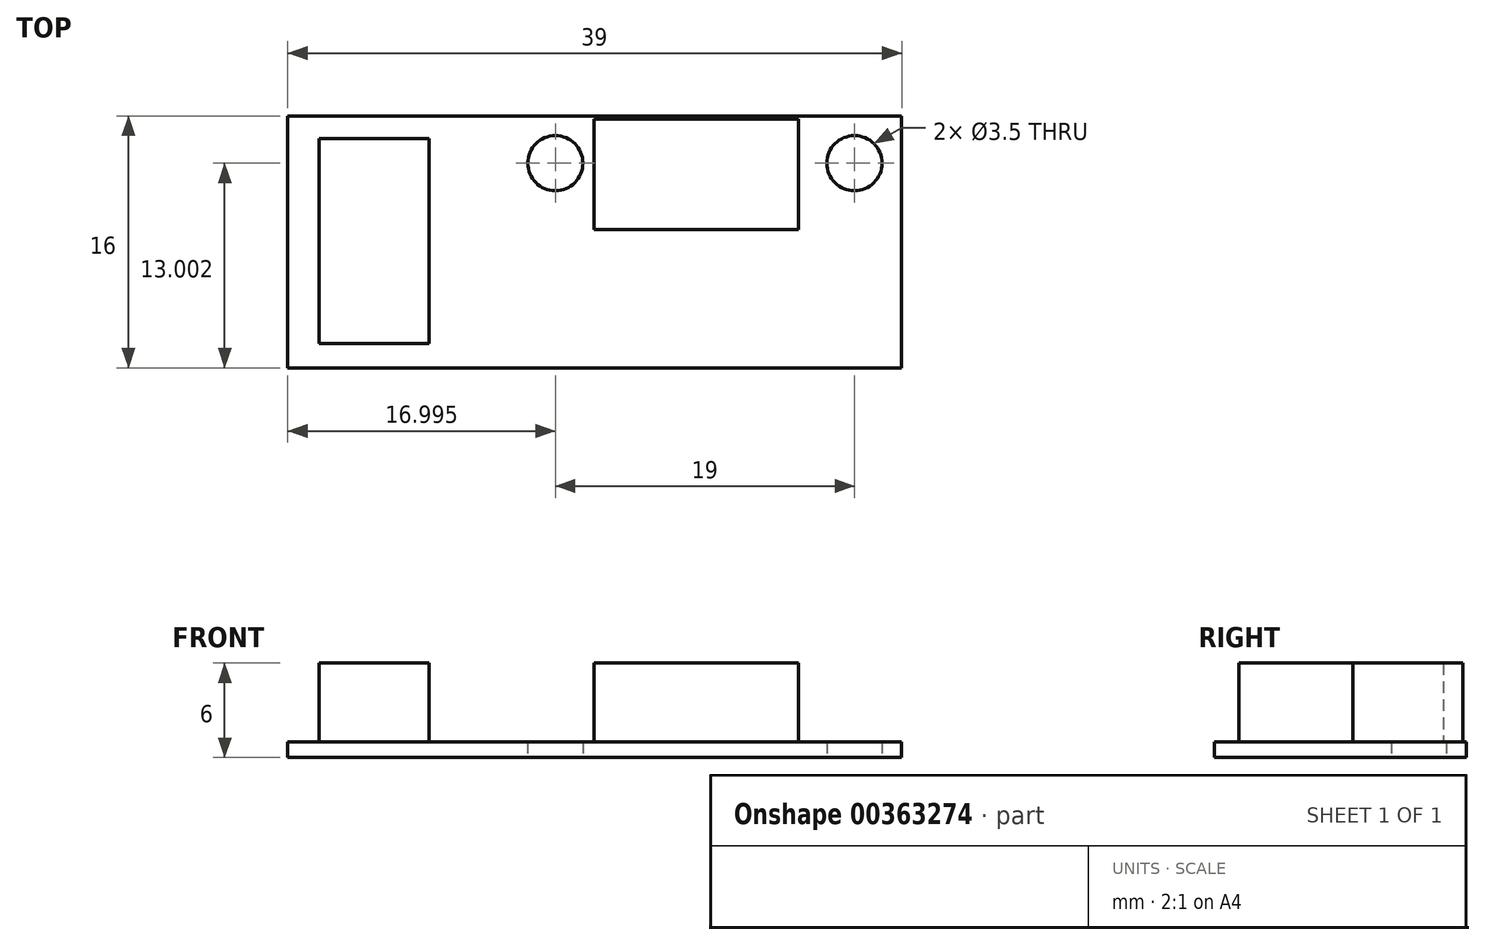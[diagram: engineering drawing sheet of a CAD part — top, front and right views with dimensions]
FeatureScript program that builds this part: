
annotation { "Feature Type Name" : "Feature", "Feature Type Description" : "" }
export const myFeature = defineFeature(function(context is Context, id is Id, definition is map)
    precondition{}
    {
        {
            var Q0;
            Q0=qCreatedBy(makeId("Top.planeOp"),FACE);
            var sketch = newSketch(context, id + "F0", { "sketchPlane" : qUnion([Q0])});
            skLineSegment(sketch, "E0.bottom", {"start": v(-16.63, 6.28) * mm, "end": v(22.37, 6.28) * mm});
            skLineSegment(sketch, "E0.top", {"start": v(-16.63, -9.72) * mm, "end": v(22.37, -9.72) * mm});
            skLineSegment(sketch, "E0.left", {"start": v(-16.63, 6.28) * mm, "end": v(-16.63, -9.72) * mm});
            skLineSegment(sketch, "E0.right", {"start": v(22.37, 6.28) * mm, "end": v(22.37, -9.72) * mm});
            skCircle(sketch, "E1", {"center": v(19.37, 3.28) * mm, "radius": 1.75 * mm});
            skCircle(sketch, "E2", {"center": v(0.37, 3.28) * mm, "radius": 1.75 * mm});
            skSolve(sketch);
        }
        {
            var Q0;
            Q0=qSketchRegion(id+"F0",true);
            extrude(context, id + "F1", {"entities" : qUnion([Q0]), "depth" : 1 * mm});
        }
        {
            var Q0;
            Q0=makeQuery(id+"F1.opExtrude","CAP_FACE",FACE,{"disambiguationData":[OSD([sQuery(id+"F0.wireOp",EDGE,"E0.bottom"),sQuery(id+"F0.wireOp",EDGE,"E0.top"),sQuery(id+"F0.wireOp",EDGE,"E0.left"),sQuery(id+"F0.wireOp",EDGE,"E0.right"),sQuery(id+"F0.wireOp",EDGE,"E1"),sQuery(id+"F0.wireOp",EDGE,"E2")])],"isStart":false});
            var sketch = newSketch(context, id + "F2", { "sketchPlane" : qUnion([Q0])});
            skLineSegment(sketch, "E3.bottom", {"start": v(2.82, 6.08) * mm, "end": v(15.82, 6.08) * mm});
            skLineSegment(sketch, "E3.top", {"start": v(2.82, -0.92) * mm, "end": v(15.82, -0.92) * mm});
            skLineSegment(sketch, "E3.left", {"start": v(2.82, 6.08) * mm, "end": v(2.82, -0.92) * mm});
            skLineSegment(sketch, "E3.right", {"start": v(15.82, 6.08) * mm, "end": v(15.82, -0.92) * mm});
            skLineSegment(sketch, "E4.bottom", {"start": v(-14.64, -8.16) * mm, "end": v(-7.64, -8.16) * mm});
            skLineSegment(sketch, "E4.top", {"start": v(-14.64, 4.84) * mm, "end": v(-7.64, 4.84) * mm});
            skLineSegment(sketch, "E4.left", {"start": v(-14.64, -8.16) * mm, "end": v(-14.64, 4.84) * mm});
            skLineSegment(sketch, "E4.right", {"start": v(-7.64, -8.16) * mm, "end": v(-7.64, 4.84) * mm});
            skPoint(sketch, "E5", {"position": v(-15.82, -1.72) * mm});
            skPoint(sketch, "E5.positionSnap0", {"position": v(-16.63, -1.72) * mm});
            skSolve(sketch);
        }
        {
            var Q0;
            Q0=qSketchRegion(id+"F2",true);
            extrude(context, id + "F3", {"entities" : qUnion([Q0]), "operationType" : NewBodyOperationType.ADD, "depth" : 5 * mm});
        }
    });
